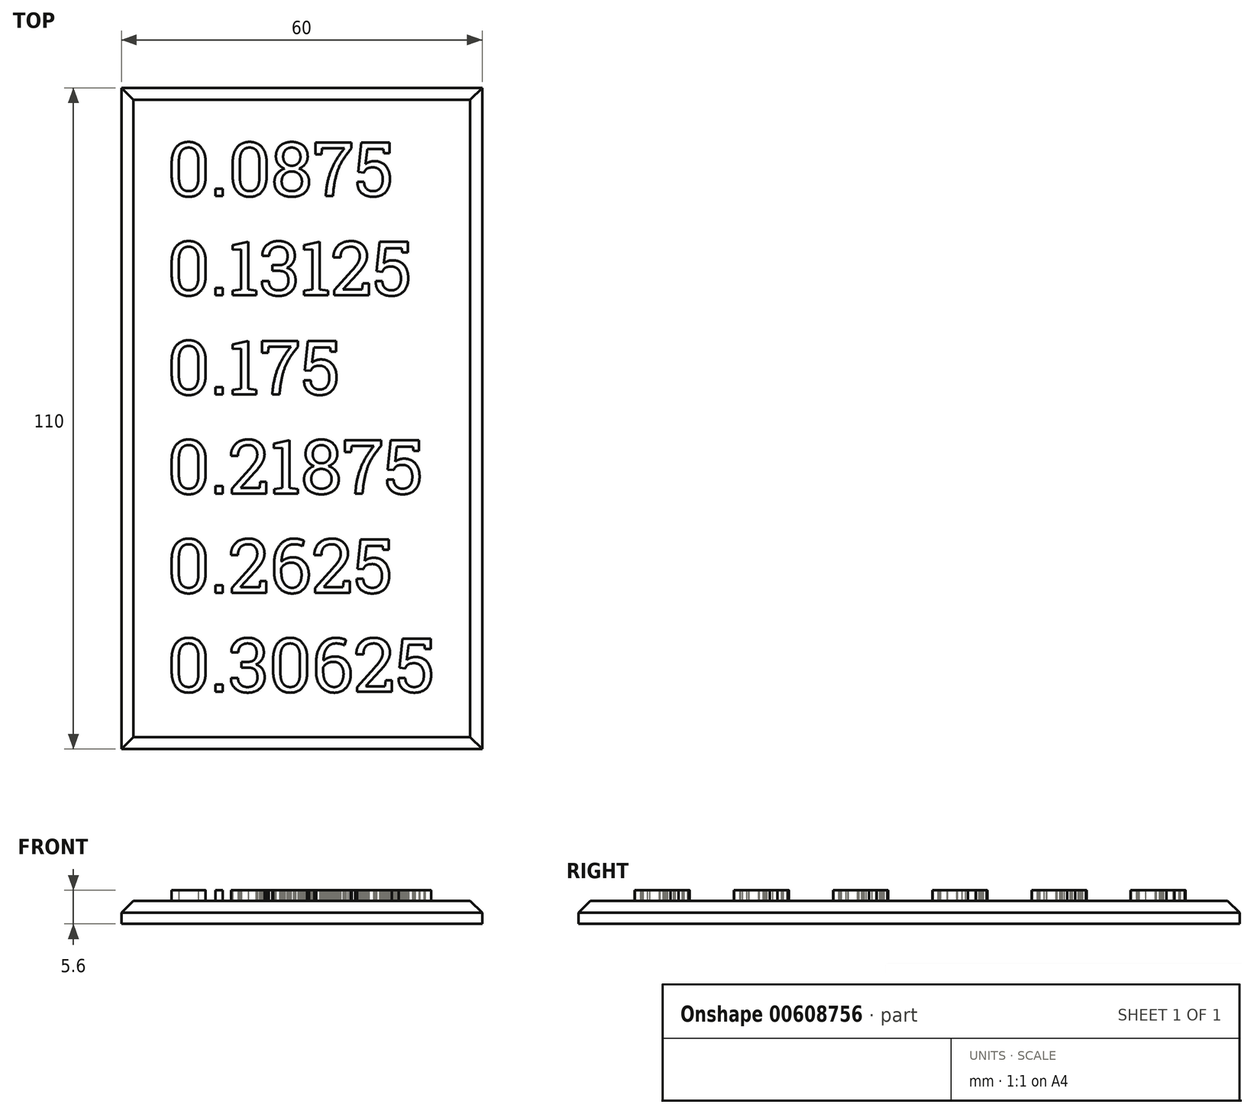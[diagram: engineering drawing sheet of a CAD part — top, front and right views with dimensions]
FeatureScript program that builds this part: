
annotation { "Feature Type Name" : "Feature", "Feature Type Description" : "" }
export const myFeature = defineFeature(function(context is Context, id is Id, definition is map)
    precondition{}
    {
        {
            var Q0;
            Q0=qCreatedBy(makeId("Top.planeOp"),FACE);
            var sketch = newSketch(context, id + "F0", { "sketchPlane" : qUnion([Q0])});
            skLineSegment(sketch, "E0.bottom", {"start": v(-35.4, 71.87) * mm, "end": v(24.6, 71.87) * mm});
            skLineSegment(sketch, "E0.top", {"start": v(-35.4, -38.13) * mm, "end": v(24.6, -38.13) * mm});
            skLineSegment(sketch, "E0.left", {"start": v(-35.4, 71.87) * mm, "end": v(-35.4, -38.13) * mm});
            skLineSegment(sketch, "E0.right", {"start": v(24.6, 71.87) * mm, "end": v(24.6, -38.13) * mm});
            skSolve(sketch);
        }
        {
            var Q0;
            Q0 = qSketchRegion(id + "F0", true);
            extrude(context, id + "F1", {"entities" : qUnion([Q0]), "depth" : 3.85 * mm, "offsetDistance" : 25 * mm});
        }
        {
            var Q0;
            Q0=makeQuery(id+"F1.opExtrude","CAP_FACE",FACE,{"disambiguationData":[OSD([sQuery(id+"F0.wireOp",EDGE,"E0.bottom"),sQuery(id+"F0.wireOp",EDGE,"E0.top"),sQuery(id+"F0.wireOp",EDGE,"E0.left"),sQuery(id+"F0.wireOp",EDGE,"E0.right")])],"isStart":false});
            var sketch = newSketch(context, id + "F2", { "sketchPlane" : qUnion([Q0])});
            skLineSegment(sketch, "E1.0", {"start": v(-35.4, 71.87) * mm, "end": v(24.6, 71.87) * mm});
            skLineSegment(sketch, "E2.0", {"start": v(24.6, 71.87) * mm, "end": v(24.6, -38.13) * mm});
            skLineSegment(sketch, "E3.0", {"start": v(-35.4, 71.87) * mm, "end": v(-35.4, -38.13) * mm});
            skText(sketch, "E4", { "text": "0.0875\n0.13125\n0.175\n0.21875\n0.2625\n0.30625", "fontName": "RobotoSlab-Regular.ttf"});
            const initialGuessF2  = {"E4": [-0.0278, 0.05387, 1, 0, 0.009]};
            skSetInitialGuess(sketch, initialGuessF2);
            skSolve(sketch);
        }
        {
            var Q0;
            Q0 = qSketchRegion(id + "F2", true);
            extrude(context, id + "F3", {"entities" : qUnion([Q0]), "operationType" : NewBodyOperationType.ADD, "depth" : 1.75 * mm, "offsetDistance" : 25 * mm});
        }
        {
            var Q0;
            Q0=makeQuery(id+"F1.opExtrude","CAP_EDGE",EDGE,{"disambiguationData":[OSD([sQuery(id+"F0.wireOp",EDGE,"E0.top")])],"isStart":false});
            var Q1;
            Q1=makeQuery(id+"F1.opExtrude","CAP_EDGE",EDGE,{"disambiguationData":[OSD([sQuery(id+"F0.wireOp",EDGE,"E0.right")])],"isStart":false});
            var Q2;
            Q2=makeQuery(id+"F1.opExtrude","CAP_EDGE",EDGE,{"disambiguationData":[OSD([sQuery(id+"F0.wireOp",EDGE,"E0.bottom")])],"isStart":false});
            var Q3;
            Q3=makeQuery(id+"F1.opExtrude","CAP_EDGE",EDGE,{"disambiguationData":[OSD([sQuery(id+"F0.wireOp",EDGE,"E0.left")])],"isStart":false});
            chamfer(context, id + "F4", {"entities" : qUnion([Q0, Q1, Q2, Q3]), "width" : 2 * mm, "tangentPropagation" : true});
        }
    });
